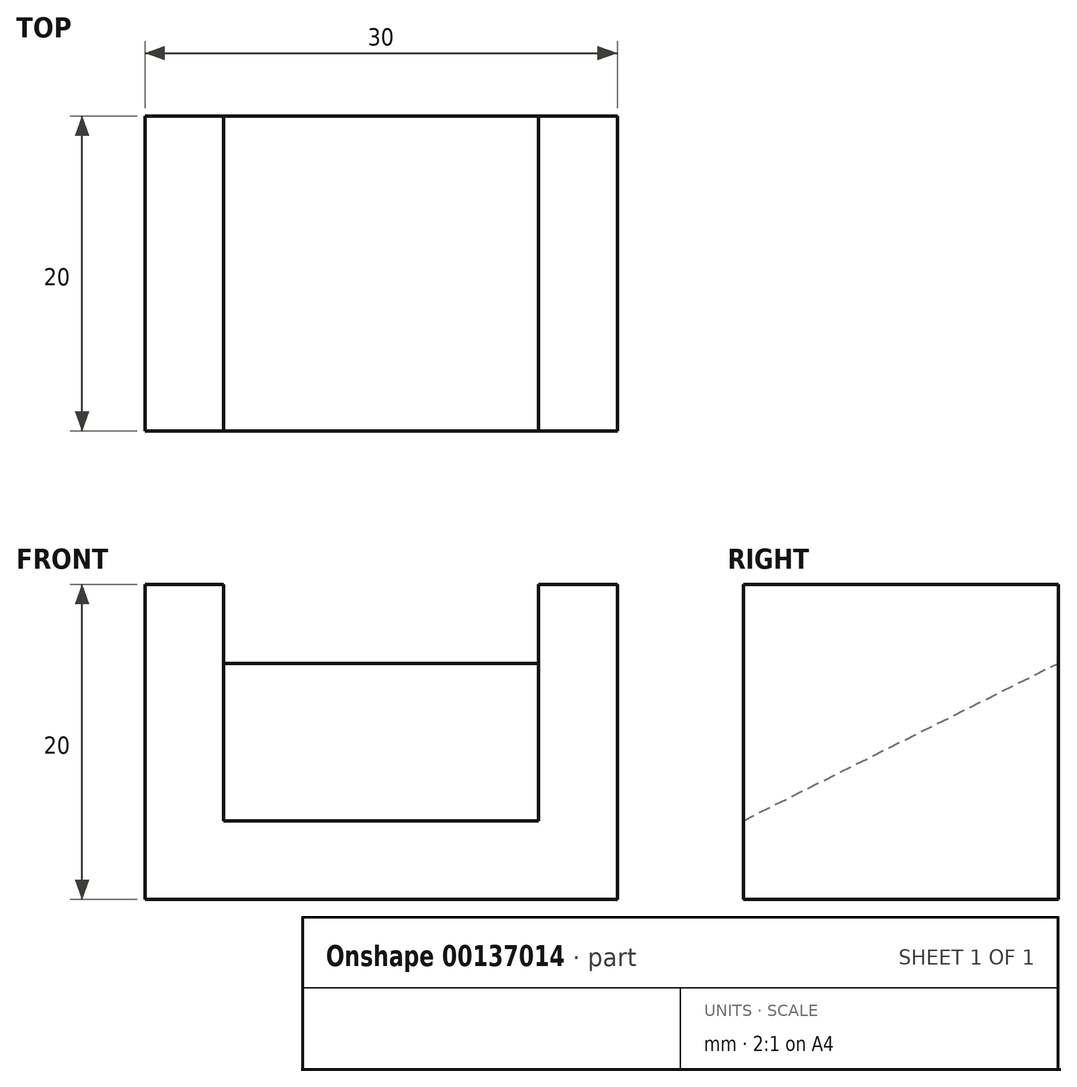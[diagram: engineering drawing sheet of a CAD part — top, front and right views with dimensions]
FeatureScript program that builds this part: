
annotation { "Feature Type Name" : "Feature", "Feature Type Description" : "" }
export const myFeature = defineFeature(function(context is Context, id is Id, definition is map)
    precondition{}
    {
        {
            var Q0;
            Q0=qCreatedBy(makeId("Right.planeOp"),FACE);
            var sketch = newSketch(context, id + "F0", { "sketchPlane" : qUnion([Q0])});
            skLineSegment(sketch, "E0", {"start": v(0, 0) * mm, "end": v(0, 5) * mm});
            skLineSegment(sketch, "E1", {"start": v(0, 5) * mm, "end": v(20, 15) * mm});
            skLineSegment(sketch, "E2", {"start": v(20, 15) * mm, "end": v(20, 0) * mm});
            skLineSegment(sketch, "E3", {"start": v(20, 0) * mm, "end": v(0, 0) * mm});
            skSolve(sketch);
        }
        {
            var Q0;
            Q0=makeQuery(id+"F0.imprint","IMPRINT",FACE,{"disambiguationData":[TD([[makeQuery(id+"F0.imprint","IMPRINT",EDGE,{"derivedFrom":sQuery(id+"F0.wireOp",EDGE,"E0")}),-1.0]])]});
            extrude(context, id + "F1", {"entities" : qUnion([Q0]), "endBound" : BoundingType.SYMMETRIC, "depth" : 20 * mm});
        }
        {
            var Q0;
            Q0=makeQuery(id+"F1.opExtrude","CAP_FACE",FACE,{"disambiguationData":[OSD([sQuery(id+"F0.wireOp",EDGE,"E0"),sQuery(id+"F0.wireOp",EDGE,"E1"),sQuery(id+"F0.wireOp",EDGE,"E2"),sQuery(id+"F0.wireOp",EDGE,"E3")])],"isStart":false});
            var sketch = newSketch(context, id + "F2", { "sketchPlane" : qUnion([Q0])});
            skLineSegment(sketch, "E4.bottom", {"start": v(0, 0) * mm, "end": v(20, 0) * mm});
            skLineSegment(sketch, "E4.top", {"start": v(0, 20) * mm, "end": v(20, 20) * mm});
            skLineSegment(sketch, "E4.left", {"start": v(0, 0) * mm, "end": v(0, 20) * mm});
            skLineSegment(sketch, "E4.right", {"start": v(20, 0) * mm, "end": v(20, 20) * mm});
            skSolve(sketch);
        }
        {
            var Q0;
            Q0 = qSketchRegion(id + "F2", true);
            extrude(context, id + "F3", {"entities" : qUnion([Q0]), "operationType" : NewBodyOperationType.ADD, "depth" : 5 * mm});
        }
        {
            var Q0;
            Q0=makeQuery(id+"F1.opExtrude","CAP_FACE",FACE,{"disambiguationData":[OSD([sQuery(id+"F0.wireOp",EDGE,"E0"),sQuery(id+"F0.wireOp",EDGE,"E1"),sQuery(id+"F0.wireOp",EDGE,"E2"),sQuery(id+"F0.wireOp",EDGE,"E3")])],"isStart":true});
            var sketch = newSketch(context, id + "F4", { "sketchPlane" : qUnion([Q0])});
            skLineSegment(sketch, "E5.bottom", {"start": v(0, 0) * mm, "end": v(-20, 0) * mm});
            skLineSegment(sketch, "E5.top", {"start": v(0, 20) * mm, "end": v(-20, 20) * mm});
            skLineSegment(sketch, "E5.left", {"start": v(0, 0) * mm, "end": v(0, 20) * mm});
            skLineSegment(sketch, "E5.right", {"start": v(-20, 0) * mm, "end": v(-20, 20) * mm});
            skSolve(sketch);
        }
        {
            var Q0;
            Q0 = qSketchRegion(id + "F4", true);
            extrude(context, id + "F5", {"entities" : qUnion([Q0]), "operationType" : NewBodyOperationType.ADD, "depth" : 5 * mm});
        }
    });
